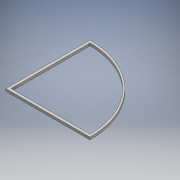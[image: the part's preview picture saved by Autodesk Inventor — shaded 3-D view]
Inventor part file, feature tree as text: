
AUTODESK INVENTOR PART (.ipt)
format: ipt  version: 2016 (Build 200138000, 138)  size: 131,584 bytes
history: native  units: mm
features: thread x4, extrude x3, sketch x3
ambient origin geometry x8: Origin, YZ Plane, XZ Plane, XY Plane, X Axis, Y Axis, Z Axis, Center Point
bodies: 实体1 (feature_tree)
feature tree (10):
  extrude  "拉伸1"  Depth=500.0mm
  extrude  "拉伸2"  Depth=15.0mm
  thread  "螺纹1"  [1 undecoded]
  thread  "螺纹2"  [1 undecoded]
  extrude  "拉伸3"  Depth=500.0mm
  thread  "螺纹3"  [1 undecoded]
  thread  "螺纹4"  [1 undecoded]
  sketch  "草图1"  dims[d0=500.0mm d1=500.0mm]
  sketch  "草图2"  dims[d2=15.0mm d3=15.0mm d4=470.0mm d5=470.0mm]
  sketch  "草图3"  dims[d6=470.0mm d7=500.0mm d8=15.0mm d9=0.0mm d10=5.0mm d11=5.0mm d12=30.0mm d13=430.0mm d14=430.0mm d15=0.0mm d16=10.0mm d17=0.0mm d18=10.0mm d19=0.0mm d20=7.5mm d21=7.5mm d22=5.0mm d23=5.0mm d24=30.0mm d25=430.0mm d26=7.5mm d27=7.5mm d28=5.0mm d29=0.0mm d30=10.0mm d31=0.0mm d32=10.0mm d33=0.0mm]
note: 4 required parameter values undecoded (feature->parameter linkage not recoverable at this tier; creation-order binding heuristic only, values carry confidence <= 0.55)
